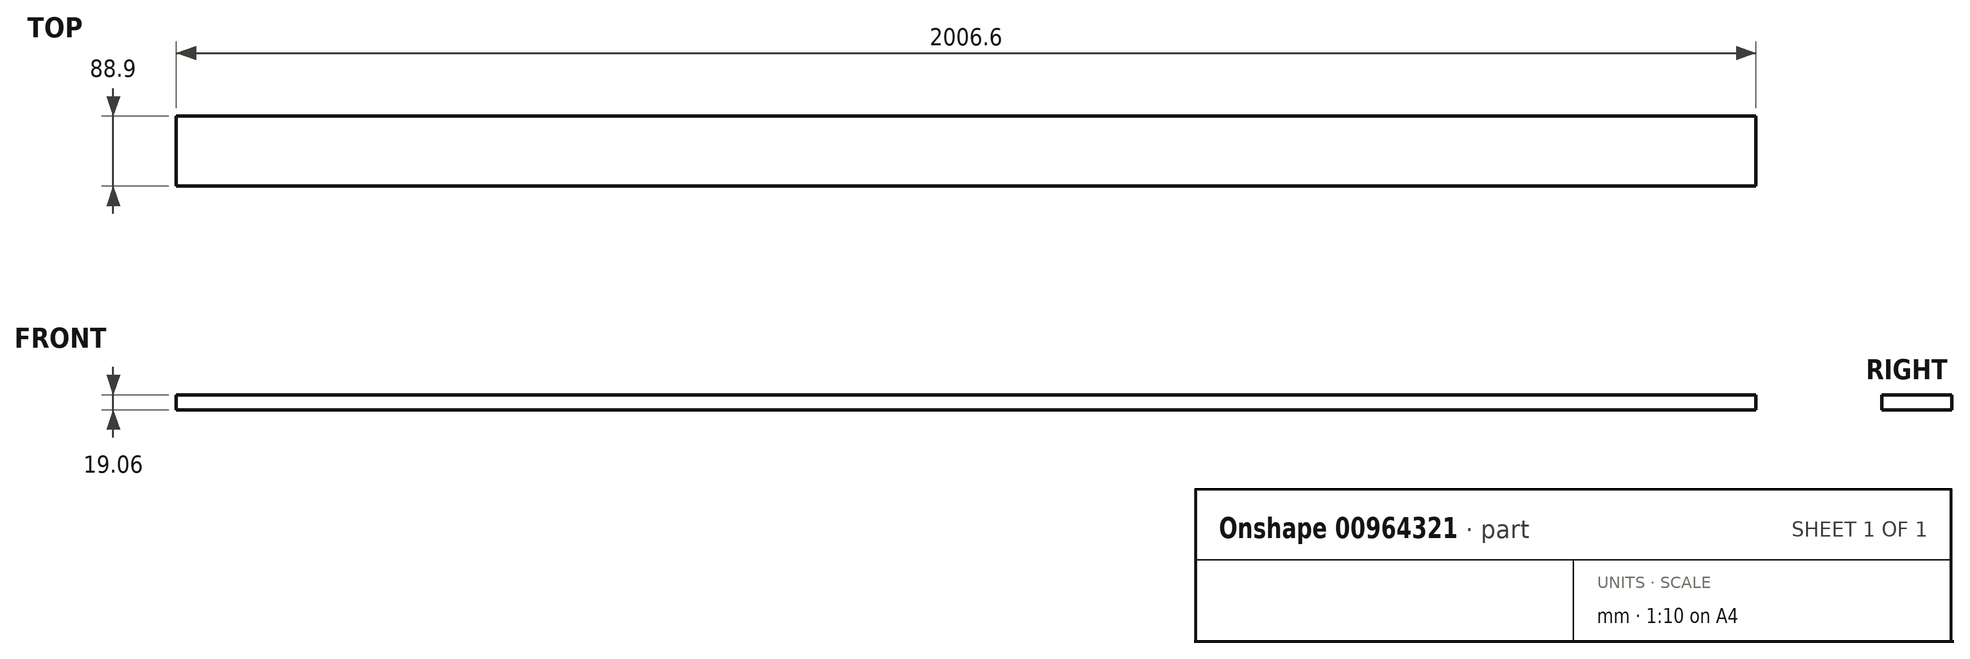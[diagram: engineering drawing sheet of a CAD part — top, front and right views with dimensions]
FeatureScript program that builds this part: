
annotation { "Feature Type Name" : "Feature", "Feature Type Description" : "" }
export const myFeature = defineFeature(function(context is Context, id is Id, definition is map)
    precondition{}
    {
        {
            var Q0;
            Q0=qCreatedBy(makeId("Right.planeOp"),FACE);
            var sketch = newSketch(context, id + "F0", { "sketchPlane" : qUnion([Q0])});
            skLineSegment(sketch, "E0.bottom", {"start": v(-44.45, 9.53) * mm, "end": v(44.45, 9.53) * mm});
            skLineSegment(sketch, "E0.top", {"start": v(-44.45, -9.53) * mm, "end": v(44.45, -9.53) * mm});
            skLineSegment(sketch, "E0.left", {"start": v(-44.45, 9.53) * mm, "end": v(-44.45, -9.53) * mm});
            skLineSegment(sketch, "E0.right", {"start": v(44.45, 9.53) * mm, "end": v(44.45, -9.53) * mm});
            skPoint(sketch, "E0.middle", {"position": v(0, 0) * mm});
            skSolve(sketch);
        }
        {
            var Q0;
            Q0=qSketchRegion(id+"F0",true);
            extrude(context, id + "F1", {"entities" : qUnion([Q0]), "endBound" : BoundingType.SYMMETRIC, "depth" : 2006.6 * mm, "offsetDistance" : 25.4 * mm});
        }
    });
